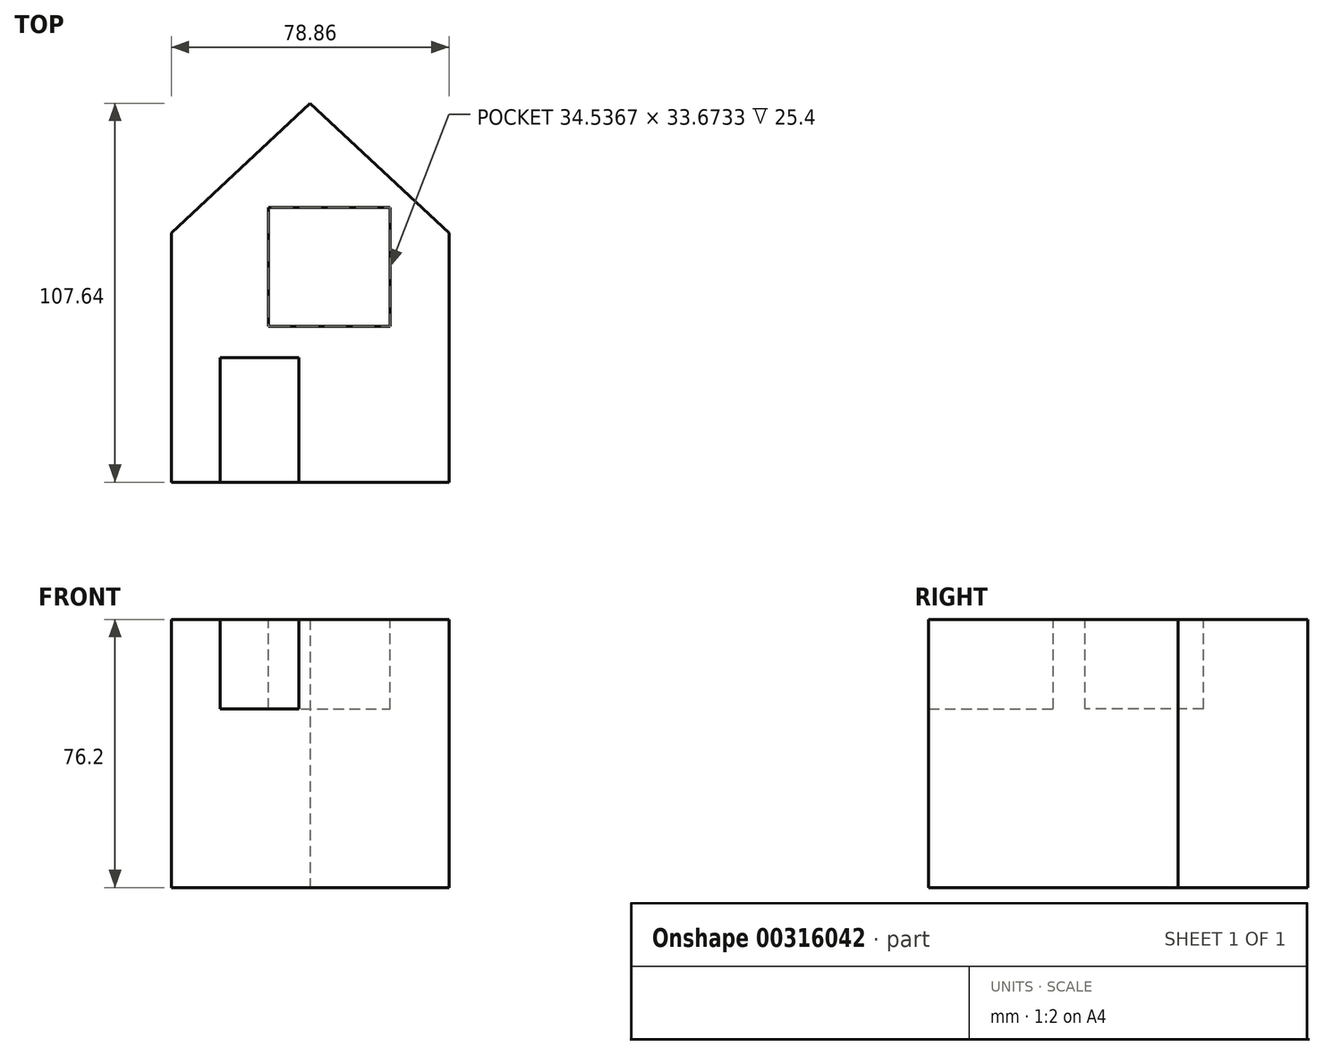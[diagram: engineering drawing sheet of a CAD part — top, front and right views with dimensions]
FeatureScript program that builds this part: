
annotation { "Feature Type Name" : "Feature", "Feature Type Description" : "" }
export const myFeature = defineFeature(function(context is Context, id is Id, definition is map)
    precondition{}
    {
        {
            var Q0;
            Q0=qCreatedBy(makeId("Top.planeOp"),FACE);
            var sketch = newSketch(context, id + "F0", { "sketchPlane" : qUnion([Q0])});
            skLineSegment(sketch, "E0.bottom", {"start": v(-39.43, 35.4) * mm, "end": v(39.43, 35.4) * mm});
            skLineSegment(sketch, "E0.top", {"start": v(-39.43, -35.4) * mm, "end": v(39.43, -35.4) * mm});
            skLineSegment(sketch, "E0.left", {"start": v(-39.43, 35.4) * mm, "end": v(-39.43, -35.4) * mm});
            skLineSegment(sketch, "E0.right", {"start": v(39.43, 35.4) * mm, "end": v(39.43, -35.4) * mm});
            skPoint(sketch, "E0.middle", {"position": v(0, 0) * mm});
            skLineSegment(sketch, "E1", {"start": v(-39.43, 35.4) * mm, "end": v(0, 72.24) * mm});
            skLineSegment(sketch, "E2", {"start": v(39.43, 35.4) * mm, "end": v(0, 72.24) * mm});
            skSolve(sketch);
        }
        {
            var Q0;
            Q0=makeQuery(id+"F0.imprint","IMPRINT",FACE,{"disambiguationData":[TD([[makeQuery(id+"F0.imprint","IMPRINT",EDGE,{"derivedFrom":sQuery(id+"F0.wireOp",EDGE,"E0.bottom")}),-1.0]])]});
            var Q1;
            Q1=makeQuery(id+"F0.imprint","IMPRINT",FACE,{"disambiguationData":[TD([[makeQuery(id+"F0.imprint","IMPRINT",EDGE,{"derivedFrom":sQuery(id+"F0.wireOp",EDGE,"E0.bottom")}),1.0]])]});
            extrude(context, id + "F1", {"entities" : qUnion([Q0, Q1]), "depth" : 76.2 * mm});
        }
        {
            var Q0;
            Q0=makeQuery(id+"F1.opExtrude","CAP_FACE",FACE,{"disambiguationData":[OSD([sQuery(id+"F0.wireOp",EDGE,"E0.top"),sQuery(id+"F0.wireOp",EDGE,"E0.left"),sQuery(id+"F0.wireOp",EDGE,"E0.right"),sQuery(id+"F0.wireOp",EDGE,"E1"),sQuery(id+"F0.wireOp",EDGE,"E2")])],"isStart":false});
            var sketch = newSketch(context, id + "F2", { "sketchPlane" : qUnion([Q0])});
            skLineSegment(sketch, "E3.bottom", {"start": v(-25.61, -35.4) * mm, "end": v(-3.17, -35.4) * mm});
            skLineSegment(sketch, "E3.top", {"start": v(-25.61, 0) * mm, "end": v(-3.17, 0) * mm});
            skLineSegment(sketch, "E3.left", {"start": v(-25.61, -35.4) * mm, "end": v(-25.61, 0) * mm});
            skLineSegment(sketch, "E3.right", {"start": v(-3.17, -35.4) * mm, "end": v(-3.17, 0) * mm});
            skSolve(sketch);
        }
        {
            var Q0;
            Q0=makeQuery(id+"F2.imprint","IMPRINT",FACE,{"disambiguationData":[TD([[makeQuery(id+"F2.imprint","IMPRINT",EDGE,{"derivedFrom":sQuery(id+"F2.wireOp",EDGE,"E3.bottom")}),1.0]])]});
            extrude(context, id + "F3", {"entities" : qUnion([Q0]), "operationType" : NewBodyOperationType.REMOVE, "oppositeDirection" : true, "depth" : 25.4 * mm});
        }
        {
            var Q0;
            Q0=makeQuery(id+"F1.opExtrude","CAP_FACE",FACE,{"disambiguationData":[OSD([sQuery(id+"F0.wireOp",EDGE,"E0.top"),sQuery(id+"F0.wireOp",EDGE,"E0.left"),sQuery(id+"F0.wireOp",EDGE,"E0.right"),sQuery(id+"F0.wireOp",EDGE,"E1"),sQuery(id+"F0.wireOp",EDGE,"E2")])],"isStart":false});
            var sketch = newSketch(context, id + "F4", { "sketchPlane" : qUnion([Q0])});
            skSolve(sketch);
        }
        {
            var Q0;
            {var subQ3=sQuery(id+"F0.wireOp",EDGE,"E0.left");Q0=makeQuery(id+"F4.imprint","IMPRINT",FACE,{"disambiguationData":[TD([[makeQuery(id+"F4.imprint","IMPRINT",EDGE,{"derivedFrom":makeQuery(id+"F1.opExtrude","CAP_EDGE",EDGE,{"disambiguationData":[OSD([subQ3])],"isStart":false})}),1.0]])]});}
            var sketch = newSketch(context, id + "F5", { "sketchPlane" : qUnion([Q0])});
            skLineSegment(sketch, "E4.bottom", {"start": v(-11.8, 42.6) * mm, "end": v(22.74, 42.6) * mm});
            skLineSegment(sketch, "E4.top", {"start": v(-11.8, 8.92) * mm, "end": v(22.74, 8.92) * mm});
            skLineSegment(sketch, "E4.left", {"start": v(-11.8, 42.6) * mm, "end": v(-11.8, 8.92) * mm});
            skLineSegment(sketch, "E4.right", {"start": v(22.74, 42.6) * mm, "end": v(22.74, 8.92) * mm});
            skSolve(sketch);
        }
        {
            var Q0;
            Q0=makeQuery(id+"F5.imprint","IMPRINT",FACE,{"disambiguationData":[TD([[makeQuery(id+"F5.imprint","IMPRINT",EDGE,{"derivedFrom":sQuery(id+"F5.wireOp",EDGE,"E4.bottom")}),-1.0]])]});
            extrude(context, id + "F6", {"entities" : qUnion([Q0]), "operationType" : NewBodyOperationType.REMOVE, "oppositeDirection" : true, "depth" : 25.4 * mm});
        }
    });
